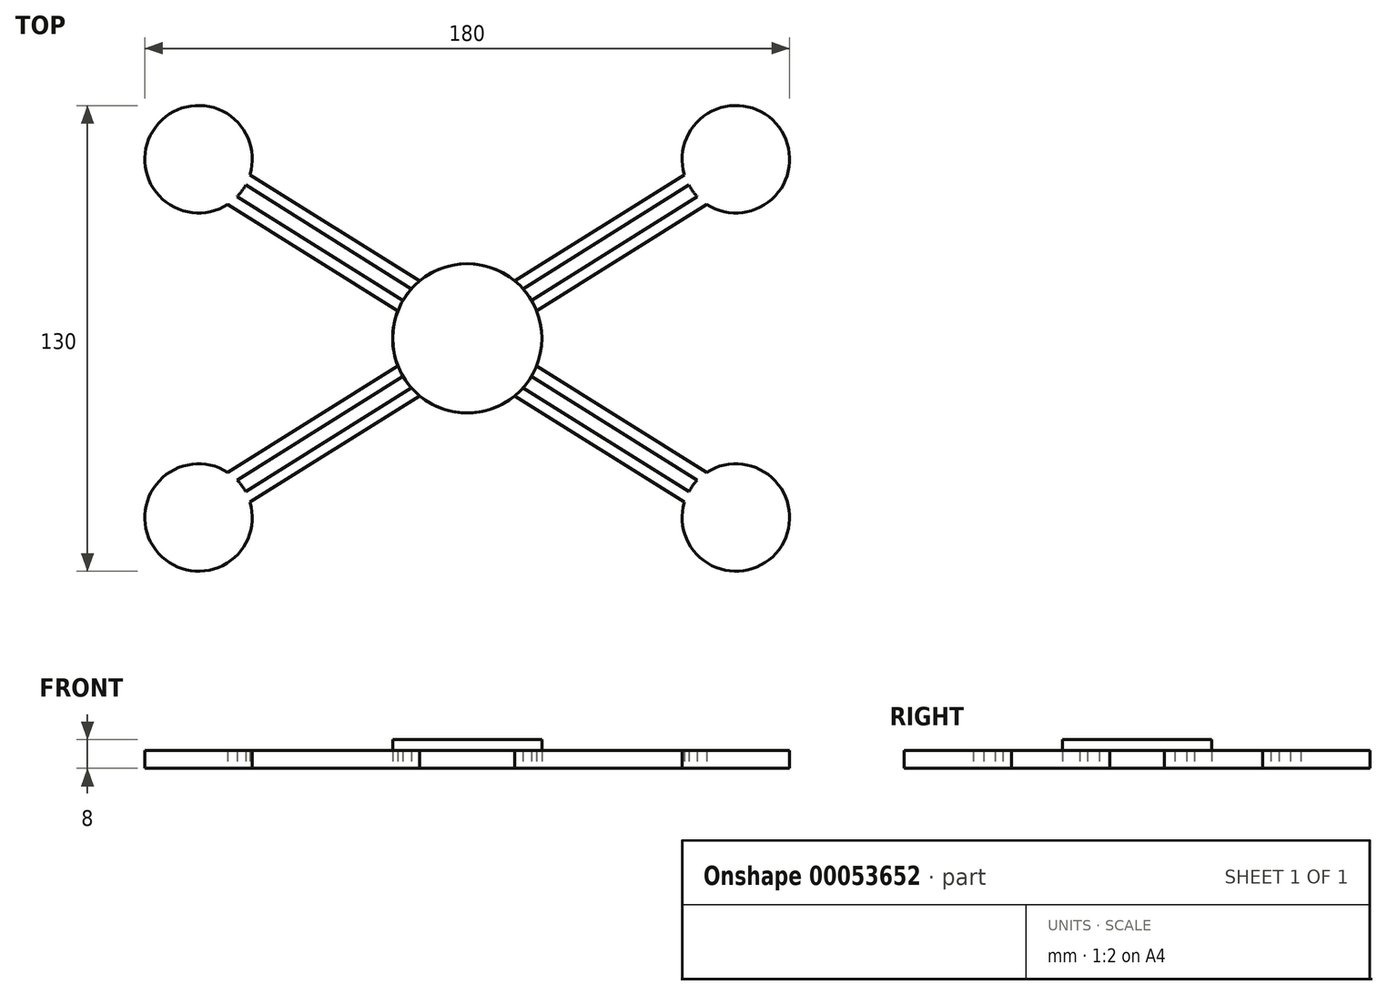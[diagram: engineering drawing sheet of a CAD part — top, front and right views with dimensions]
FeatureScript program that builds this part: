
annotation { "Feature Type Name" : "Feature", "Feature Type Description" : "" }
export const myFeature = defineFeature(function(context is Context, id is Id, definition is map)
    precondition{}
    {
        {
            var Q0;
            Q0=qCreatedBy(makeId("Top.planeOp"),FACE);
            var sketch = newSketch(context, id + "F0", { "sketchPlane" : qUnion([Q0])});
            skCircle(sketch, "E0", {"center": v(6.46, -4.31) * mm, "radius": 20.82 * mm});
            skLineSegment(sketch, "E1.rect.bottom", {"start": v(81.46, -54.31) * mm, "end": v(-68.54, -54.31) * mm});
            skLineSegment(sketch, "E1.rect.top", {"start": v(81.46, 45.69) * mm, "end": v(-68.54, 45.69) * mm});
            skLineSegment(sketch, "E1.rect.left", {"start": v(81.46, -54.31) * mm, "end": v(81.46, 45.69) * mm});
            skLineSegment(sketch, "E1.rect.right", {"start": v(-68.54, -54.31) * mm, "end": v(-68.54, 45.69) * mm});
            skCircle(sketch, "E2", {"center": v(-68.54, 45.69) * mm, "radius": 15 * mm});
            skCircle(sketch, "E3.MirrorC", {"center": v(-68.54, -54.31) * mm, "radius": 15 * mm});
            skCircle(sketch, "E4.MirrorC", {"center": v(81.46, 45.69) * mm, "radius": 15 * mm});
            skCircle(sketch, "E5.MirrorC", {"center": v(81.46, -54.31) * mm, "radius": 15 * mm});
            skPoint(sketch, "E6", {"position": v(-68.54, 38.19) * mm});
            skPoint(sketch, "E7.MirrorP", {"position": v(81.46, 38.19) * mm});
            skPoint(sketch, "E8.MirrorP", {"position": v(-68.54, -46.81) * mm});
            skPoint(sketch, "E9.MirrorP", {"position": v(81.46, -46.81) * mm});
            skPoint(sketch, "E10", {"position": v(-61.04, 45.69) * mm});
            skPoint(sketch, "E11.MirrorP", {"position": v(73.96, 45.69) * mm});
            skPoint(sketch, "E12.MirrorP", {"position": v(-61.04, -54.31) * mm});
            skPoint(sketch, "E13.MirrorP", {"position": v(73.96, -54.31) * mm});
            skLineSegment(sketch, "E14", {"start": v(-68.54, -46.81) * mm, "end": v(-12.9, -11.98) * mm});
            skLineSegment(sketch, "E15", {"start": v(-61.04, -54.31) * mm, "end": v(-6.8, -20.36) * mm});
            skLineSegment(sketch, "E16.MirrorCS", {"start": v(73.96, -54.31) * mm, "end": v(19.73, -20.36) * mm});
            skLineSegment(sketch, "E17.MirrorCS", {"start": v(81.46, -46.81) * mm, "end": v(25.82, -11.98) * mm});
            skLineSegment(sketch, "E18.MirrorCS", {"start": v(-61.04, 45.69) * mm, "end": v(-6.8, 11.74) * mm});
            skLineSegment(sketch, "E19.MirrorCS", {"start": v(-68.54, 38.19) * mm, "end": v(-12.9, 3.36) * mm});
            skLineSegment(sketch, "E20.MirrorCS", {"start": v(73.96, 45.69) * mm, "end": v(19.73, 11.74) * mm});
            skLineSegment(sketch, "E21.MirrorCS", {"start": v(81.46, 38.19) * mm, "end": v(25.82, 3.36) * mm});
            skLineSegment(sketch, "E22", {"start": v(-61.04, 45.69) * mm, "end": v(-12.9, 3.36) * mm, "construction": true});
            skLineSegment(sketch, "E23", {"start": v(-6.8, 11.74) * mm, "end": v(-68.54, 38.19) * mm, "construction": true});
            skPoint(sketch, "E24", {"position": v(-37.27, 24.8) * mm});
            skLineSegment(sketch, "E25", {"start": v(-10.37, 7.95) * mm, "end": v(-56.45, 36.8) * mm});
            skLineSegment(sketch, "E26.MirrorCS", {"start": v(23.3, 7.95) * mm, "end": v(69.38, 36.8) * mm});
            skLineSegment(sketch, "E27.MirrorCS", {"start": v(-10.37, -16.57) * mm, "end": v(-56.45, -45.42) * mm});
            skLineSegment(sketch, "E28.MirrorCS", {"start": v(23.3, -16.57) * mm, "end": v(69.38, -45.42) * mm});
            skPoint(sketch, "E29", {"position": v(-55.38, 38.49) * mm});
            skPoint(sketch, "E30", {"position": v(-57.74, 35.27) * mm});
            skPoint(sketch, "E31", {"position": v(-9.11, 9.5) * mm});
            skPoint(sketch, "E32", {"position": v(-11.46, 6.28) * mm});
            skLineSegment(sketch, "E33", {"start": v(-57.74, 35.27) * mm, "end": v(-11.46, 6.28) * mm});
            skLineSegment(sketch, "E34", {"start": v(-9.11, 9.5) * mm, "end": v(-55.38, 38.49) * mm});
            skLineSegment(sketch, "E35.MirrorCS", {"start": v(22.04, 9.5) * mm, "end": v(68.3, 38.49) * mm});
            skLineSegment(sketch, "E36.MirrorCS", {"start": v(70.67, 35.27) * mm, "end": v(24.4, 6.28) * mm});
            skLineSegment(sketch, "E37.MirrorCS", {"start": v(-57.74, -43.9) * mm, "end": v(-11.46, -14.9) * mm});
            skLineSegment(sketch, "E38.MirrorCS", {"start": v(-9.11, -18.13) * mm, "end": v(-55.38, -47.1) * mm});
            skLineSegment(sketch, "E39.MirrorCS", {"start": v(22.04, -18.13) * mm, "end": v(68.3, -47.1) * mm});
            skLineSegment(sketch, "E40.MirrorCS", {"start": v(70.67, -43.9) * mm, "end": v(24.4, -14.9) * mm});
            skSolve(sketch);
        }
        {
            var Q0;
            {var subQ0=sQuery(id+"F0.wireOp",EDGE,"E0");var subQ3=makeQuery(id+"F0.imprint","INTERSECT",VERTEX,{"derivedFrom":[subQ0,sQuery(id+"F0.wireOp",EDGE,"E21.MirrorCS")]});Q0=makeQuery(id+"F0.imprint","IMPRINT",FACE,{"disambiguationData":[TD([[makeQuery(id+"F0.imprint","IMPRINT",EDGE,{"disambiguationData":[TD([[subQ3,-1.0]])],"derivedFrom":subQ0}),1.0]])]});}
            extrude(context, id + "F1", {"entities" : qUnion([Q0]), "depth" : 8 * mm});
        }
        {
            var Q0;
            {var subQ3=sQuery(id+"F0.wireOp",EDGE,"E36.MirrorCS");Q0=makeQuery(id+"F0.imprint","IMPRINT",FACE,{"disambiguationData":[TD([[makeQuery(id+"F0.imprint","IMPRINT",EDGE,{"derivedFrom":subQ3}),1.0]])]});}
            var Q1;
            {var subQ3=sQuery(id+"F0.wireOp",EDGE,"E35.MirrorCS");Q1=makeQuery(id+"F0.imprint","IMPRINT",FACE,{"disambiguationData":[TD([[makeQuery(id+"F0.imprint","IMPRINT",EDGE,{"derivedFrom":subQ3}),1.0]])]});}
            var Q2;
            {var subQ0=sQuery(id+"F0.wireOp",EDGE,"E1.rect.left");var subQ1=sQuery(id+"F0.wireOp",EDGE,"E1.rect.top");var subQ2=makeQuery(id+"F0.imprint","INTERSECT",VERTEX,{"derivedFrom":[subQ1,subQ0]});Q2=makeQuery(id+"F0.imprint","IMPRINT",FACE,{"disambiguationData":[TD([[makeQuery(id+"F0.imprint","IMPRINT",EDGE,{"disambiguationData":[TD([[subQ2,-1.0]])],"derivedFrom":subQ1}),-1.0]])]});}
            var Q3;
            {var subQ3=sQuery(id+"F0.wireOp",EDGE,"E1.rect.left");var subQ4=sQuery(id+"F0.wireOp",EDGE,"E1.rect.top");var subQ5=makeQuery(id+"F0.imprint","INTERSECT",VERTEX,{"derivedFrom":[subQ4,subQ3]});Q3=makeQuery(id+"F0.imprint","IMPRINT",FACE,{"disambiguationData":[TD([[makeQuery(id+"F0.imprint","IMPRINT",EDGE,{"disambiguationData":[TD([[subQ5,-1.0]])],"derivedFrom":subQ4}),1.0]])]});}
            var Q4;
            {var subQ0=sQuery(id+"F0.wireOp",EDGE,"E21.MirrorCS");var subQ1=sQuery(id+"F0.wireOp",EDGE,"E1.rect.left");var subQ2=makeQuery(id+"F0.imprint","INTERSECT",VERTEX,{"derivedFrom":[subQ1,subQ0]});Q4=makeQuery(id+"F0.imprint","IMPRINT",FACE,{"disambiguationData":[TD([[makeQuery(id+"F0.imprint","IMPRINT",EDGE,{"disambiguationData":[TD([[subQ2,1.0]])],"derivedFrom":subQ1}),1.0]])]});}
            var Q5;
            {var subQ0=sQuery(id+"F0.wireOp",EDGE,"E20.MirrorCS");var subQ1=sQuery(id+"F0.wireOp",EDGE,"E1.rect.top");var subQ2=makeQuery(id+"F0.imprint","INTERSECT",VERTEX,{"derivedFrom":[subQ1,subQ0]});Q5=makeQuery(id+"F0.imprint","IMPRINT",FACE,{"disambiguationData":[TD([[makeQuery(id+"F0.imprint","IMPRINT",EDGE,{"disambiguationData":[TD([[subQ2,-1.0]])],"derivedFrom":subQ1}),1.0]])]});}
            var Q6;
            {var subQ1=sQuery(id+"F0.wireOp",EDGE,"E1.rect.top");var subQ6=makeQuery(id+"F0.imprint","INTERSECT",VERTEX,{"derivedFrom":[subQ1,sQuery(id+"F0.wireOp",EDGE,"E18.MirrorCS")]});Q6=makeQuery(id+"F0.imprint","IMPRINT",FACE,{"disambiguationData":[TD([[makeQuery(id+"F0.imprint","IMPRINT",EDGE,{"disambiguationData":[TD([[subQ6,1.0]])],"derivedFrom":subQ1}),-1.0]])]});}
            var Q7;
            {var subQ0=sQuery(id+"F0.wireOp",EDGE,"E1.rect.right");var subQ1=sQuery(id+"F0.wireOp",EDGE,"E1.rect.top");var subQ2=makeQuery(id+"F0.imprint","INTERSECT",VERTEX,{"derivedFrom":[subQ1,subQ0]});Q7=makeQuery(id+"F0.imprint","IMPRINT",FACE,{"disambiguationData":[TD([[makeQuery(id+"F0.imprint","IMPRINT",EDGE,{"disambiguationData":[TD([[subQ2,1.0]])],"derivedFrom":subQ1}),1.0]])]});}
            var Q8;
            {var subQ0=sQuery(id+"F0.wireOp",EDGE,"E18.MirrorCS");var subQ1=sQuery(id+"F0.wireOp",EDGE,"E1.rect.top");var subQ2=makeQuery(id+"F0.imprint","INTERSECT",VERTEX,{"derivedFrom":[subQ1,subQ0]});Q8=makeQuery(id+"F0.imprint","IMPRINT",FACE,{"disambiguationData":[TD([[makeQuery(id+"F0.imprint","IMPRINT",EDGE,{"disambiguationData":[TD([[subQ2,1.0]])],"derivedFrom":subQ1}),1.0]])]});}
            var Q9;
            {var subQ0=sQuery(id+"F0.wireOp",EDGE,"E19.MirrorCS");var subQ1=sQuery(id+"F0.wireOp",EDGE,"E1.rect.right");var subQ2=makeQuery(id+"F0.imprint","INTERSECT",VERTEX,{"derivedFrom":[subQ1,subQ0]});Q9=makeQuery(id+"F0.imprint","IMPRINT",FACE,{"disambiguationData":[TD([[makeQuery(id+"F0.imprint","IMPRINT",EDGE,{"disambiguationData":[TD([[subQ2,1.0]])],"derivedFrom":subQ1}),-1.0]])]});}
            var Q10;
            {var subQ3=sQuery(id+"F0.wireOp",EDGE,"E33");Q10=makeQuery(id+"F0.imprint","IMPRINT",FACE,{"disambiguationData":[TD([[makeQuery(id+"F0.imprint","IMPRINT",EDGE,{"derivedFrom":subQ3}),-1.0]])]});}
            var Q11;
            {var subQ3=sQuery(id+"F0.wireOp",EDGE,"E34");Q11=makeQuery(id+"F0.imprint","IMPRINT",FACE,{"disambiguationData":[TD([[makeQuery(id+"F0.imprint","IMPRINT",EDGE,{"derivedFrom":subQ3}),-1.0]])]});}
            var Q12;
            {var subQ0=sQuery(id+"F0.wireOp",EDGE,"E0");var subQ3=makeQuery(id+"F0.imprint","INTERSECT",VERTEX,{"derivedFrom":[subQ0,sQuery(id+"F0.wireOp",EDGE,"E21.MirrorCS")]});Q12=makeQuery(id+"F0.imprint","IMPRINT",FACE,{"disambiguationData":[TD([[makeQuery(id+"F0.imprint","IMPRINT",EDGE,{"disambiguationData":[TD([[subQ3,-1.0]])],"derivedFrom":subQ0}),1.0]])]});}
            var Q13;
            {var subQ3=sQuery(id+"F0.wireOp",EDGE,"E37.MirrorCS");Q13=makeQuery(id+"F0.imprint","IMPRINT",FACE,{"disambiguationData":[TD([[makeQuery(id+"F0.imprint","IMPRINT",EDGE,{"derivedFrom":subQ3}),1.0]])]});}
            var Q14;
            {var subQ3=sQuery(id+"F0.wireOp",EDGE,"E38.MirrorCS");Q14=makeQuery(id+"F0.imprint","IMPRINT",FACE,{"disambiguationData":[TD([[makeQuery(id+"F0.imprint","IMPRINT",EDGE,{"derivedFrom":subQ3}),1.0]])]});}
            var Q15;
            {var subQ3=sQuery(id+"F0.wireOp",EDGE,"E39.MirrorCS");Q15=makeQuery(id+"F0.imprint","IMPRINT",FACE,{"disambiguationData":[TD([[makeQuery(id+"F0.imprint","IMPRINT",EDGE,{"derivedFrom":subQ3}),-1.0]])]});}
            var Q16;
            {var subQ3=sQuery(id+"F0.wireOp",EDGE,"E40.MirrorCS");Q16=makeQuery(id+"F0.imprint","IMPRINT",FACE,{"disambiguationData":[TD([[makeQuery(id+"F0.imprint","IMPRINT",EDGE,{"derivedFrom":subQ3}),-1.0]])]});}
            var Q17;
            {var subQ0=sQuery(id+"F0.wireOp",EDGE,"E1.rect.left");var subQ4=sQuery(id+"F0.wireOp",EDGE,"E1.rect.bottom");var subQ5=makeQuery(id+"F0.imprint","INTERSECT",VERTEX,{"derivedFrom":[subQ4,subQ0]});Q17=makeQuery(id+"F0.imprint","IMPRINT",FACE,{"disambiguationData":[TD([[makeQuery(id+"F0.imprint","IMPRINT",EDGE,{"disambiguationData":[TD([[subQ5,-1.0]])],"derivedFrom":subQ4}),1.0]])]});}
            var Q18;
            {var subQ4=sQuery(id+"F0.wireOp",EDGE,"E1.rect.left");var subQ5=sQuery(id+"F0.wireOp",EDGE,"E1.rect.bottom");var subQ6=makeQuery(id+"F0.imprint","INTERSECT",VERTEX,{"derivedFrom":[subQ5,subQ4]});Q18=makeQuery(id+"F0.imprint","IMPRINT",FACE,{"disambiguationData":[TD([[makeQuery(id+"F0.imprint","IMPRINT",EDGE,{"disambiguationData":[TD([[subQ6,-1.0]])],"derivedFrom":subQ5}),-1.0]])]});}
            var Q19;
            {var subQ0=sQuery(id+"F0.wireOp",EDGE,"E17.MirrorCS");var subQ1=sQuery(id+"F0.wireOp",EDGE,"E1.rect.left");var subQ2=makeQuery(id+"F0.imprint","INTERSECT",VERTEX,{"derivedFrom":[subQ1,subQ0]});Q19=makeQuery(id+"F0.imprint","IMPRINT",FACE,{"disambiguationData":[TD([[makeQuery(id+"F0.imprint","IMPRINT",EDGE,{"disambiguationData":[TD([[subQ2,-1.0]])],"derivedFrom":subQ1}),1.0]])]});}
            var Q20;
            {var subQ0=sQuery(id+"F0.wireOp",EDGE,"E16.MirrorCS");var subQ1=sQuery(id+"F0.wireOp",EDGE,"E1.rect.bottom");var subQ2=makeQuery(id+"F0.imprint","INTERSECT",VERTEX,{"derivedFrom":[subQ1,subQ0]});Q20=makeQuery(id+"F0.imprint","IMPRINT",FACE,{"disambiguationData":[TD([[makeQuery(id+"F0.imprint","IMPRINT",EDGE,{"disambiguationData":[TD([[subQ2,-1.0]])],"derivedFrom":subQ1}),-1.0]])]});}
            var Q21;
            {var subQ4=sQuery(id+"F0.wireOp",EDGE,"E1.rect.bottom");var subQ6=makeQuery(id+"F0.imprint","INTERSECT",VERTEX,{"derivedFrom":[subQ4,sQuery(id+"F0.wireOp",EDGE,"E15")]});Q21=makeQuery(id+"F0.imprint","IMPRINT",FACE,{"disambiguationData":[TD([[makeQuery(id+"F0.imprint","IMPRINT",EDGE,{"disambiguationData":[TD([[subQ6,1.0]])],"derivedFrom":subQ4}),1.0]])]});}
            var Q22;
            {var subQ5=sQuery(id+"F0.wireOp",EDGE,"E1.rect.right");var subQ6=sQuery(id+"F0.wireOp",EDGE,"E1.rect.bottom");var subQ7=makeQuery(id+"F0.imprint","INTERSECT",VERTEX,{"derivedFrom":[subQ6,subQ5]});Q22=makeQuery(id+"F0.imprint","IMPRINT",FACE,{"disambiguationData":[TD([[makeQuery(id+"F0.imprint","IMPRINT",EDGE,{"disambiguationData":[TD([[subQ7,1.0]])],"derivedFrom":subQ6}),-1.0]])]});}
            var Q23;
            {var subQ0=sQuery(id+"F0.wireOp",EDGE,"E14");var subQ1=sQuery(id+"F0.wireOp",EDGE,"E1.rect.right");var subQ2=makeQuery(id+"F0.imprint","INTERSECT",VERTEX,{"derivedFrom":[subQ1,subQ0]});Q23=makeQuery(id+"F0.imprint","IMPRINT",FACE,{"disambiguationData":[TD([[makeQuery(id+"F0.imprint","IMPRINT",EDGE,{"disambiguationData":[TD([[subQ2,-1.0]])],"derivedFrom":subQ1}),-1.0]])]});}
            var Q24;
            {var subQ0=sQuery(id+"F0.wireOp",EDGE,"E15");var subQ1=sQuery(id+"F0.wireOp",EDGE,"E1.rect.bottom");var subQ2=makeQuery(id+"F0.imprint","INTERSECT",VERTEX,{"derivedFrom":[subQ1,subQ0]});Q24=makeQuery(id+"F0.imprint","IMPRINT",FACE,{"disambiguationData":[TD([[makeQuery(id+"F0.imprint","IMPRINT",EDGE,{"disambiguationData":[TD([[subQ2,1.0]])],"derivedFrom":subQ1}),-1.0]])]});}
            extrude(context, id + "F2", {"entities" : qUnion([Q0, Q1, Q2, Q3, Q4, Q5, Q6, Q7, Q8, Q9, Q10, Q11, Q12, Q13, Q14, Q15, Q16, Q17, Q18, Q19, Q20, Q21, Q22, Q23, Q24]), "depth" : 5 * mm});
        }
    });
